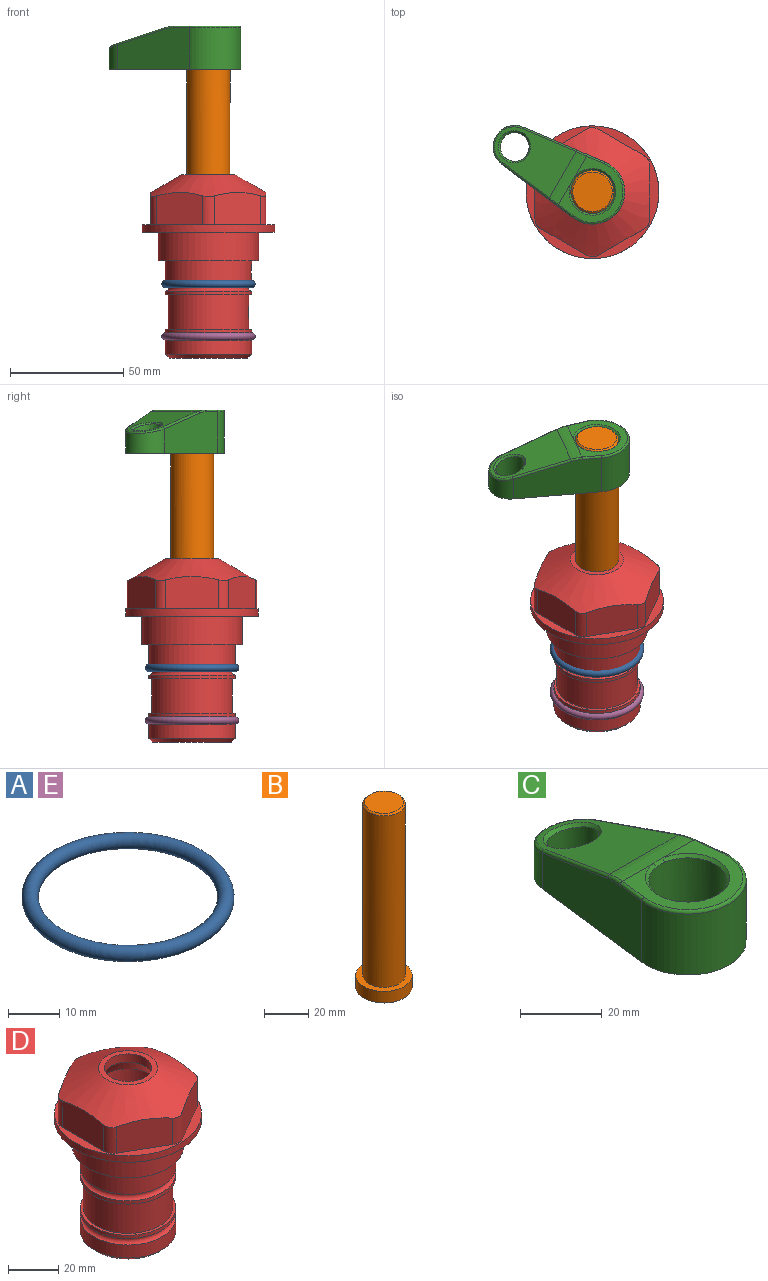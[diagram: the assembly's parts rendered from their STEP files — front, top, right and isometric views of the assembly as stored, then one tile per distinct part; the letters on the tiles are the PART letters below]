
ASSEMBLY  parts=5 mates=4
PART A: 1 faces, bbox 44.7x44.7x3.2 mm
  f0: torus R=19.05mm, axis (0,0,1), area 1193.9mm2
PART B: 6 faces, bbox 25.4x25.4x101.6 mm
  f0: plane 17.46x17.46mm, normal (0,0,1), area 239.5mm2, adj f5
  f1: plane 25.4x25.4mm, normal (0,0,-1), area 506.7mm2, adj f2
  f2: cylinder r=12.7mm len=25.4mm, axis (0,0,1), area 506.7mm2, adj f1,f3
  f3: plane 25.4x25.4mm, normal (0,0,1), area 221.7mm2, adj f2,f4
  f4: cylinder r=9.53mm len=94.46mm, axis (0,0,1), area 5653mm2, adj f3,f5
  f5: cone r=8.73mm half-angle=45deg, axis (0,0,-1), area 64.4mm2, adj f0,f4
PART C: 31 faces, bbox 31.7x65.5x19.8 mm
  f0: plane 39.12x18.26mm, normal (0.99,0.12,0), area 612.2mm2, adj f1,f4,f7,f11,f13,f15
  f1: cylinder r=9.53mm len=18.91mm, axis (0,0,-1), area 296.1mm2, adj f0,f2,f7,f17
  f2: plane 39.12x18.26mm, normal (-0.99,0.12,0), area 612.2mm2, adj f1,f4,f7,f12,f14,f16
  f3: cylinder r=6.35mm len=12.7mm, axis (0,0,-1), area 362.4mm2, adj f7,f18
  f4: cylinder r=14.29mm len=28.58mm, axis (0,0,-1), area 882.2mm2, adj f0,f2,f7,f10
  f5: cylinder r=9.53mm len=19.05mm, axis (0,0,-1), area 1092.6mm2, adj f7,f19,f20
  f6: plane 26.99x23.69mm, normal (0,0,1), area 216.2mm2, adj f9,f10,f11,f12,f19
  f7: plane 63.5x28.58mm, normal (0,0,-1), area 661.8mm2, adj f0,f1,f2,f3,f4,f5,f22,f23
  f8: plane 33.52x23.6mm, normal (0,0.26,0.97), area 486mm2, adj f9,f15,f16,f17,f18
  f9: cylinder r=19.05mm len=24.72mm, axis (1,0,0), area 120.4mm2, adj f6,f8,f13,f14,f20
  f10: torus R=13.49mm, axis (0,0,1), area 59mm2, adj f4,f6,f11,f12
  f11: cylinder r=0.79mm len=8.67mm, axis (0.12,-0.99,0), area 10.8mm2, adj f0,f6,f10,f13
  f12: cylinder r=0.79mm len=8.67mm, axis (0.12,0.99,0), area 10.8mm2, adj f2,f6,f10,f14
  f13: bspline ~4.95x1.42mm, area 6.1mm2, adj f0,f9,f11,f15
  f14: bspline ~4.95x1.42mm, area 6.1mm2, adj f2,f9,f12,f16
  f15: cylinder r=0.79mm len=25.95mm, axis (0.12,-0.96,0.26), area 32.9mm2, adj f0,f8,f13,f17
  f16: cylinder r=0.79mm len=25.95mm, axis (0.12,0.96,-0.26), area 32.9mm2, adj f2,f8,f14,f17
  f17: bspline ~18.91x8.38mm, area 30mm2, adj f1,f8,f15,f16
  f18: bspline ~14.29x14.29mm, area 48.3mm2, adj f3,f8
  f19: cone r=9.53mm half-angle=45deg, axis (0,0,1), area 66.5mm2, adj f5,f6,f20
  f20: bspline ~3.22x0.96mm, area 3.5mm2, adj f5,f9,f19
  f21: plane 2.75x2.72mm, normal (0,0,-1), area 2.9mm2, adj f23,f25,f28
  f22: plane 23.05x15.88mm, normal (-0.99,-0.12,0), area 323.6mm2, adj f7,f25,f26,f27,f28,f29
  f23: plane 23.05x15.88mm, normal (0.99,-0.12,0), area 323.6mm2, adj f7,f21,f25,f27,f28,f30
  f24: cylinder r=9.53mm len=10.69mm, axis (0,0,-1), area 114.7mm2, adj f7,f27,f29,f30
  f25: cylinder r=12.7mm len=20.59mm, axis (0,0,-1), area 381.1mm2, adj f7,f21,f22,f23,f26,f28
  f26: plane 2.75x2.72mm, normal (0,0,-1), area 2.9mm2, adj f22,f25,f28
  f27: plane 19.72x18.37mm, normal (0,-0.26,-0.97), area 291.8mm2, adj f22,f23,f24,f28,f29,f30
  f28: cylinder r=15.88mm len=19.92mm, axis (1,0,0), area 54.8mm2, adj f21,f22,f23,f25,f26,f27
  f29: cylinder r=1.59mm len=11mm, axis (0,0,-1), area 34.7mm2, adj f7,f22,f24,f27
  f30: cylinder r=1.59mm len=11mm, axis (0,0,-1), area 34.7mm2, adj f7,f23,f24,f27
PART D: 36 faces, bbox 58.7x58.7x81 mm
  f0: cylinder r=17.78mm len=35.56mm, axis (0,0,1), area 1670.8mm2, adj f23,f24,f31
  f1: cylinder r=19.05mm len=38.1mm, axis (0,0,1), area 1191.9mm2, adj f26,f27,f30
  f2: plane 58.66x58.66mm, normal (0,0,-1), area 1150.6mm2, adj f3,f28
  f3: cylinder r=29.33mm len=58.66mm, axis (0,0,-1), area 585.1mm2, adj f2,f4
  f4: plane 58.66x58.66mm, normal (0,0,1), area 475.9mm2, adj f3,f5,f6,f7,f8,f9,f10,f11
  f5: plane 20.32x14.34mm, normal (-0.5,0.87,0), area 324.4mm2, adj f4,f15,f16,f17
  f6: plane 20.32x14.34mm, normal (0.5,0.87,0), area 324.4mm2, adj f4,f14,f15,f17
  f7: plane 23.48x14.34mm, normal (1,0,0), area 324.4mm2, adj f4,f13,f14,f17
  f8: plane 20.32x14.34mm, normal (0.5,-0.87,0), area 324.4mm2, adj f4,f12,f13,f17
  f9: plane 20.32x14.34mm, normal (-0.5,-0.87,0), area 324.4mm2, adj f4,f11,f12,f17
  f10: plane 23.48x14.34mm, normal (-1,0,0), area 324.4mm2, adj f4,f11,f16,f17
  f11: cylinder r=5.08mm len=12.85mm, axis (0,0,-1), area 67.2mm2, adj f4,f9,f10,f17
  f12: cylinder r=5.08mm len=12.85mm, axis (0,0,-1), area 67.2mm2, adj f4,f8,f9,f17
  f13: cylinder r=5.08mm len=12.85mm, axis (0,0,-1), area 67.2mm2, adj f4,f7,f8,f17
  f14: cylinder r=5.08mm len=12.85mm, axis (0,0,-1), area 67.2mm2, adj f4,f6,f7,f17
  f15: cylinder r=5.08mm len=12.85mm, axis (0,0,-1), area 67.2mm2, adj f4,f5,f6,f17
  f16: cylinder r=5.08mm len=12.85mm, axis (0,0,-1), area 67.2mm2, adj f4,f5,f10,f17
  f17: cone r=11.73mm half-angle=60deg, axis (0,0,-1), area 2071.8mm2, adj f5,f6,f7,f8,f9,f10,f11,f12
  f18: plane 23.46x23.46mm, normal (0,0,1), area 147.4mm2, adj f17,f35
  f19: plane 34.93x34.93mm, normal (0,0,-1), area 958mm2, adj f29
  f20: cylinder r=19.05mm len=38.1mm, axis (0,0,1), area 760.1mm2, adj f21,f29
  f21: torus R=19.05mm, axis (0,0,1), area 565.3mm2, adj f20,f22
  f22: cylinder r=19.05mm len=38.1mm, axis (0,0,1), area 190mm2, adj f21,f23
  f23: plane 38.1x38.1mm, normal (0,0,1), area 146.9mm2, adj f0,f22
  f24: plane 38.1x38.1mm, normal (0,0,-1), area 146.9mm2, adj f0,f25
  f25: cylinder r=19.05mm len=38.1mm, axis (0,0,1), area 190mm2, adj f24,f26
  f26: torus R=19.05mm, axis (0,0,1), area 565.3mm2, adj f1,f25
  f27: plane 44.45x44.45mm, normal (0,0,-1), area 411.7mm2, adj f1,f28
  f28: cylinder r=22.23mm len=44.45mm, axis (0,0,1), area 1773.5mm2, adj f2,f27
  f29: cone r=19.05mm half-angle=45deg, axis (0,0,1), area 257.5mm2, adj f19,f20
  f30: cylinder r=3.17mm len=6.75mm, axis (-1,0,0), area 128mm2, adj f1,f33
  f31: cylinder r=3.17mm len=6.35mm, axis (-1,0,0), area 102.5mm2, adj f0,f33
  f32: plane 25.4x25.4mm, normal (0,0,1), area 506.7mm2, adj f33
  f33: cylinder r=12.7mm len=66.42mm, axis (0,0,-1), area 5236.2mm2, adj f30,f31,f32,f34
  f34: cone r=9.53mm half-angle=30deg, axis (0,0,-1), area 443.4mm2, adj f33,f35
  f35: cylinder r=9.53mm len=19.05mm, axis (0,0,-1), area 240.9mm2, adj f18,f34
PART E: same geometry as A
PLACE A t=(0,0,1.59)mm
PLACE B rot(axis=(0,0,1),60deg) t=(0,0,27.55)mm
PLACE C rot(axis=(0,0,1),60deg) t=(0,0,27.55)mm
PLACE D at identity fixed
PLACE E t=(0,0,-21.59)mm
MATE fastened B.f2 <-> C.f4  axis (0,0,-1) through (0,0,90.26)mm
MATE fastened D.f0 <-> A.f0  axis (0,0,1) through (0,0,-22.92)mm
MATE fastened D.f0 <-> E.f0  axis (0,0,1) through (0,0,-46.1)mm
MATE cylindrical B.f2 <-> D.f0  axis (0,0,-1) through (0,0,-10.55)mm
